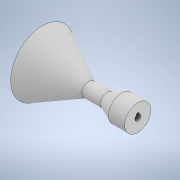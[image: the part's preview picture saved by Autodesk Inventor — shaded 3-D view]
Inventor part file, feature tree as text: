
AUTODESK INVENTOR PART (.ipt)
format: ipt  version: 2021.2 (Build 252289000, 289)  size: 126,976 bytes
history: native  units: in
note: dims shown in document units (in); Inventor stores cm internally (conversion verified against a paired STEP export)
features: sketch x2, revolve x1, extrude x1
ambient origin geometry x8: Origin, YZ Plane, XZ Plane, XY Plane, X Axis, Y Axis, Z Axis, Center Point
bodies: Solid1 (feature_tree)
feature tree (4):
  revolve  "Revolution1"  [1 undecoded]
  extrude  "Extrusion1"  Depth=0.375in
  sketch  "Sketch1"  dims[d0=1.7in d6=0.875in]
  sketch  "Sketch2"  dims[d14=0.1575in d17=0.375in d18=0.7in d21=1.0in d22=2.5in d23=90.0deg d24=0.125in d25=0.125in d26=0.0in d27=0.0in d29=0.75in]
note: 1 required parameter value undecoded (feature->parameter linkage not recoverable at this tier; creation-order binding heuristic only, values carry confidence <= 0.55)
